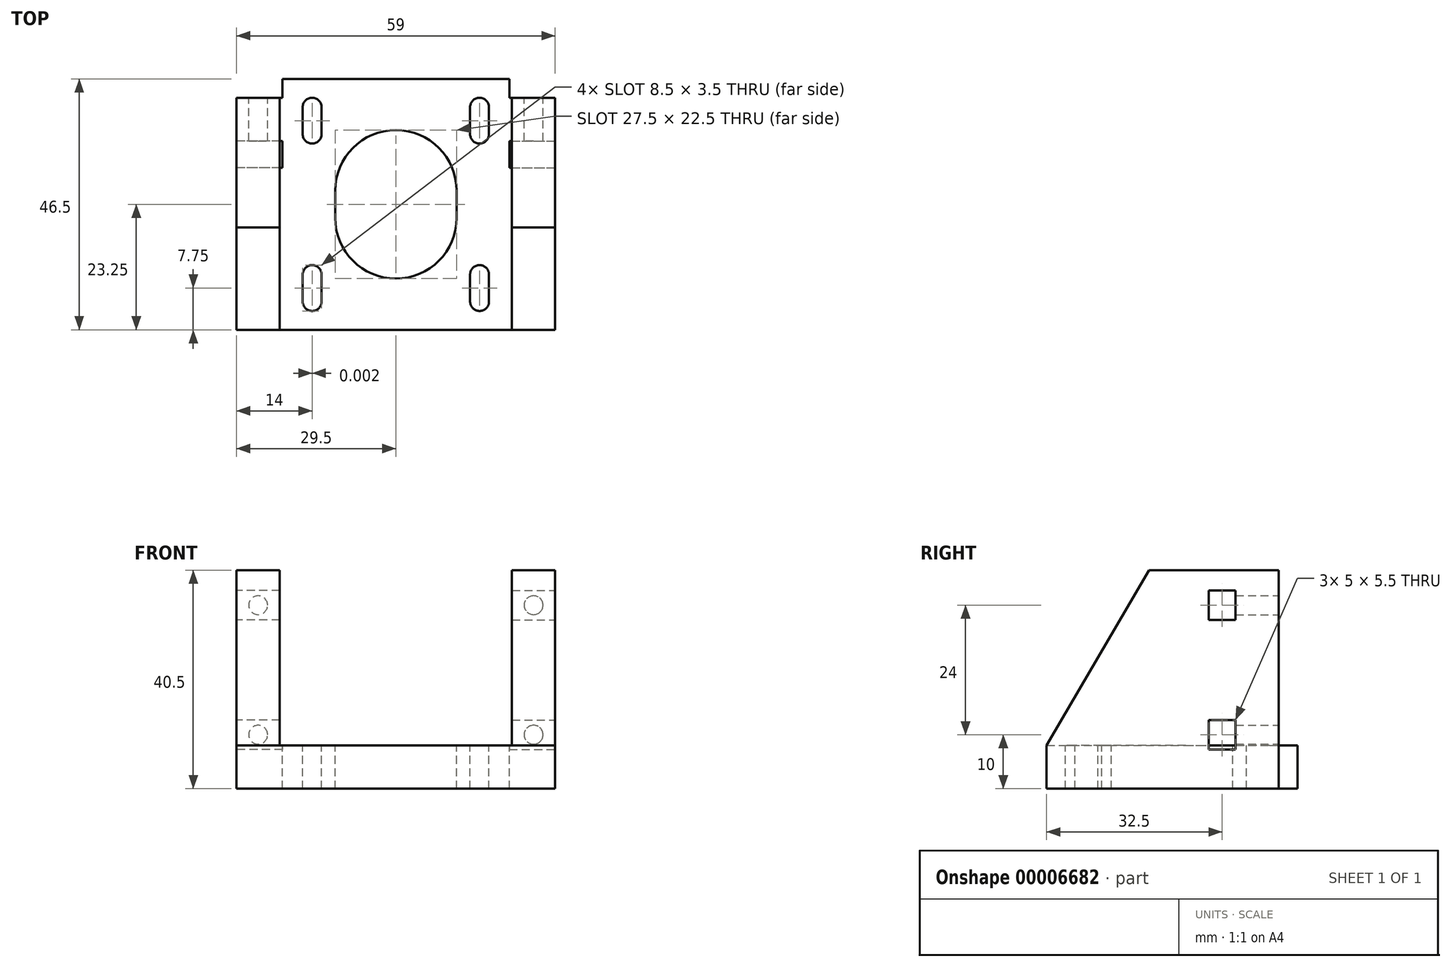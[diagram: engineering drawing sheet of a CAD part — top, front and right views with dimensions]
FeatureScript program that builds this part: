
annotation { "Feature Type Name" : "Feature", "Feature Type Description" : "" }
export const myFeature = defineFeature(function(context is Context, id is Id, definition is map)
    precondition{}
    {
        {
            var Q0;
            Q0=qCreatedBy(makeId("Top.planeOp"),FACE);
            var sketch = newSketch(context, id + "F0", { "sketchPlane" : qUnion([Q0])});
            skLineSegment(sketch, "E0.bottom", {"start": v(0, 0) * mm, "end": v(59, 0) * mm});
            skLineSegment(sketch, "E0.top", {"start": v(0, 46.5) * mm, "end": v(59, 46.5) * mm});
            skLineSegment(sketch, "E0.left", {"start": v(0, 0) * mm, "end": v(0, 46.5) * mm});
            skLineSegment(sketch, "E0.right", {"start": v(59, 0) * mm, "end": v(59, 46.5) * mm});
            skSolve(sketch);
        }
        {
            var Q0;
            Q0 = qSketchRegion(id + "F0", true);
            extrude(context, id + "F1", {"entities" : qUnion([Q0]), "depth" : 40.5 * mm});
        }
        {
            var Q0;
            Q0=makeQuery(id+"F1.opExtrude","CAP_FACE",FACE,{"disambiguationData":[OSD([sQuery(id+"F0.wireOp",EDGE,"E0.bottom"),sQuery(id+"F0.wireOp",EDGE,"E0.top"),sQuery(id+"F0.wireOp",EDGE,"E0.left"),sQuery(id+"F0.wireOp",EDGE,"E0.right")])],"isStart":false});
            var sketch = newSketch(context, id + "F2", { "sketchPlane" : qUnion([Q0])});
            skLineSegment(sketch, "E1.bottom", {"start": v(8, 0) * mm, "end": v(51, 0) * mm});
            skLineSegment(sketch, "E1.top", {"start": v(8, 46.5) * mm, "end": v(51, 46.5) * mm});
            skLineSegment(sketch, "E1.left", {"start": v(8, 0) * mm, "end": v(8, 46.5) * mm});
            skLineSegment(sketch, "E1.right", {"start": v(51, 0) * mm, "end": v(51, 46.5) * mm});
            skSolve(sketch);
        }
        {
            var Q0;
            Q0 = qSketchRegion(id + "F2", true);
            extrude(context, id + "F3", {"entities" : qUnion([Q0]), "operationType" : NewBodyOperationType.REMOVE, "oppositeDirection" : true, "depth" : 32.5 * mm});
        }
        {
            var Q0;
            Q0=makeQuery(id+"F1.opExtrude","SWEPT_FACE",FACE,{"disambiguationData":[OSD([sQuery(id+"F0.wireOp",EDGE,"E0.right")])]});
            var sketch = newSketch(context, id + "F4", { "sketchPlane" : qUnion([Q0])});
            skLineSegment(sketch, "E2", {"start": v(0, 8) * mm, "end": v(19, 40.5) * mm});
            skLineSegment(sketch, "E3", {"start": v(19, 40.5) * mm, "end": v(0, 40.5) * mm});
            skLineSegment(sketch, "E4", {"start": v(0, 40.5) * mm, "end": v(0, 8) * mm});
            skSolve(sketch);
        }
        {
            var Q0;
            Q0 = qSketchRegion(id + "F4", true);
            extrude(context, id + "F5", {"entities" : qUnion([Q0]), "operationType" : NewBodyOperationType.REMOVE, "endBound" : BoundingType.THROUGH_ALL, "oppositeDirection" : true, "depth" : 25 * mm});
        }
        {
            var Q0;
            {var subQ0=sQuery(id+"F0.wireOp",EDGE,"E0.bottom");var subQ1=sQuery(id+"F0.wireOp",EDGE,"E0.top");var subQ2=sQuery(id+"F0.wireOp",EDGE,"E0.left");Q0=makeQuery(id+"F3.boolean.opBoolean","SPLIT",FACE,{"disambiguationData":[TD([makeQuery(id+"F1.opExtrude","SWEPT_FACE",FACE,{"disambiguationData":[OSD([subQ2])]})])],"derivedFrom":makeQuery(id+"F1.opExtrude","CAP_FACE",FACE,{"disambiguationData":[OSD([subQ0,subQ1,subQ2,sQuery(id+"F0.wireOp",EDGE,"E0.right")])],"isStart":false})});}
            var sketch = newSketch(context, id + "F6", { "sketchPlane" : qUnion([Q0])});
            skLineSegment(sketch, "E5.bottom", {"start": v(0, 46.5) * mm, "end": v(8.5, 46.5) * mm});
            skLineSegment(sketch, "E5.top", {"start": v(0, 43) * mm, "end": v(8.5, 43) * mm});
            skLineSegment(sketch, "E5.left", {"start": v(0, 46.5) * mm, "end": v(0, 43) * mm});
            skLineSegment(sketch, "E5.right", {"start": v(8.5, 46.5) * mm, "end": v(8.5, 43) * mm});
            skSolve(sketch);
        }
        {
            var Q0;
            Q0 = qSketchRegion(id + "F6", true);
            extrude(context, id + "F7", {"entities" : qUnion([Q0]), "operationType" : NewBodyOperationType.REMOVE, "endBound" : BoundingType.THROUGH_ALL, "oppositeDirection" : true, "depth" : 25 * mm});
        }
        {
            var Q0;
            {var subQ0=sQuery(id+"F0.wireOp",EDGE,"E0.bottom");var subQ1=sQuery(id+"F0.wireOp",EDGE,"E0.top");var subQ2=sQuery(id+"F0.wireOp",EDGE,"E0.right");Q0=makeQuery(id+"F3.boolean.opBoolean","SPLIT",FACE,{"disambiguationData":[TD([makeQuery(id+"F1.opExtrude","SWEPT_FACE",FACE,{"disambiguationData":[OSD([subQ2])]})])],"derivedFrom":makeQuery(id+"F1.opExtrude","CAP_FACE",FACE,{"disambiguationData":[OSD([subQ0,subQ1,sQuery(id+"F0.wireOp",EDGE,"E0.left"),subQ2])],"isStart":false})});}
            var sketch = newSketch(context, id + "F8", { "sketchPlane" : qUnion([Q0])});
            skLineSegment(sketch, "E6.bottom", {"start": v(59, 46.5) * mm, "end": v(50.5, 46.5) * mm});
            skLineSegment(sketch, "E6.top", {"start": v(59, 43) * mm, "end": v(50.5, 43) * mm});
            skLineSegment(sketch, "E6.left", {"start": v(59, 46.5) * mm, "end": v(59, 43) * mm});
            skLineSegment(sketch, "E6.right", {"start": v(50.5, 46.5) * mm, "end": v(50.5, 43) * mm});
            skSolve(sketch);
        }
        {
            var Q0;
            Q0 = qSketchRegion(id + "F8", true);
            extrude(context, id + "F9", {"entities" : qUnion([Q0]), "operationType" : NewBodyOperationType.REMOVE, "endBound" : BoundingType.THROUGH_ALL, "oppositeDirection" : true, "depth" : 25 * mm});
        }
        {
            var Q0;
            Q0=makeQuery(id+"F1.opExtrude","SWEPT_FACE",FACE,{"disambiguationData":[OSD([sQuery(id+"F0.wireOp",EDGE,"E0.right")])]});
            var sketch = newSketch(context, id + "F10", { "sketchPlane" : qUnion([Q0])});
            skLineSegment(sketch, "E7.bottom", {"start": v(30, 36.75) * mm, "end": v(35, 36.75) * mm});
            skLineSegment(sketch, "E7.top", {"start": v(30, 7.25) * mm, "end": v(35, 7.25) * mm});
            skLineSegment(sketch, "E7.left", {"start": v(30, 36.75) * mm, "end": v(30, 31.25) * mm});
            skLineSegment(sketch, "E7.right", {"start": v(35, 36.75) * mm, "end": v(35, 31.25) * mm});
            skLineSegment(sketch, "E8.0", {"start": v(30, 31.25) * mm, "end": v(35, 31.25) * mm});
            skLineSegment(sketch, "E9.0", {"start": v(30, 12.75) * mm, "end": v(35, 12.75) * mm});
            skLineSegment(sketch, "E10.trimOffspring", {"start": v(30, 12.75) * mm, "end": v(30, 7.25) * mm});
            skLineSegment(sketch, "E11.trimOffspring", {"start": v(35, 12.75) * mm, "end": v(35, 7.25) * mm});
            skSolve(sketch);
        }
        {
            var Q0;
            Q0 = qSketchRegion(id + "F10", true);
            extrude(context, id + "F11", {"entities" : qUnion([Q0]), "operationType" : NewBodyOperationType.REMOVE, "oppositeDirection" : true, "depth" : 8.5 * mm});
        }
        {
            var Q0;
            Q0=makeQuery(id+"F1.opExtrude","SWEPT_FACE",FACE,{"disambiguationData":[OSD([sQuery(id+"F0.wireOp",EDGE,"E0.left")])]});
            var sketch = newSketch(context, id + "F12", { "sketchPlane" : qUnion([Q0])});
            skLineSegment(sketch, "E12.bottom", {"start": v(-35, 36.75) * mm, "end": v(-30, 36.75) * mm});
            skLineSegment(sketch, "E12.top", {"start": v(-35, 7.25) * mm, "end": v(-30, 7.25) * mm});
            skLineSegment(sketch, "E12.left", {"start": v(-35, 36.75) * mm, "end": v(-35, 31.25) * mm});
            skLineSegment(sketch, "E12.right", {"start": v(-30, 36.75) * mm, "end": v(-30, 31.25) * mm});
            skLineSegment(sketch, "E13.0", {"start": v(-35, 31.25) * mm, "end": v(-30, 31.25) * mm});
            skLineSegment(sketch, "E14.0", {"start": v(-35, 12.75) * mm, "end": v(-30, 12.75) * mm});
            skLineSegment(sketch, "E15.trimOffspring", {"start": v(-35, 12.75) * mm, "end": v(-35, 7.25) * mm});
            skLineSegment(sketch, "E16.trimOffspring", {"start": v(-30, 12.75) * mm, "end": v(-30, 7.25) * mm});
            skSolve(sketch);
        }
        {
            var Q0;
            Q0 = qSketchRegion(id + "F12", true);
            extrude(context, id + "F13", {"entities" : qUnion([Q0]), "operationType" : NewBodyOperationType.REMOVE, "oppositeDirection" : true, "depth" : 8.5 * mm});
        }
        {
            var Q0;
            Q0=makeQuery(id+"F9.boolean.opBoolean","COPY",FACE,{"derivedFrom":makeQuery(id+"F9.opExtrude","SWEPT_FACE",FACE,{"disambiguationData":[OSD([sQuery(id+"F8.wireOp",EDGE,"E6.top")])]})});
            var sketch = newSketch(context, id + "F14", { "sketchPlane" : qUnion([Q0])});
            skCircle(sketch, "E17", {"center": v(-55, 10) * mm, "radius": 1.75 * mm});
            skCircle(sketch, "E18", {"center": v(-55, 34) * mm, "radius": 1.75 * mm});
            skSolve(sketch);
        }
        {
            var Q0;
            Q0 = qSketchRegion(id + "F14", true);
            extrude(context, id + "F15", {"entities" : qUnion([Q0]), "operationType" : NewBodyOperationType.REMOVE, "oppositeDirection" : true, "depth" : 10 * mm});
        }
        {
            var Q0;
            Q0=makeQuery(id+"F7.boolean.opBoolean","COPY",FACE,{"derivedFrom":makeQuery(id+"F7.opExtrude","SWEPT_FACE",FACE,{"disambiguationData":[OSD([sQuery(id+"F6.wireOp",EDGE,"E5.top")])]})});
            var sketch = newSketch(context, id + "F16", { "sketchPlane" : qUnion([Q0])});
            skCircle(sketch, "E19", {"center": v(-4, 34) * mm, "radius": 1.75 * mm});
            skCircle(sketch, "E20", {"center": v(-4, 10) * mm, "radius": 1.75 * mm});
            skSolve(sketch);
        }
        {
            var Q0;
            Q0 = qSketchRegion(id + "F16", true);
            extrude(context, id + "F17", {"entities" : qUnion([Q0]), "operationType" : NewBodyOperationType.REMOVE, "oppositeDirection" : true, "depth" : 10 * mm});
        }
        {
            var Q0;
            Q0=makeQuery(id+"F3.boolean.opBoolean","COPY",FACE,{"derivedFrom":makeQuery(id+"F3.opExtrude","CAP_FACE",FACE,{"disambiguationData":[OSD([sQuery(id+"F2.wireOp",EDGE,"E1.bottom"),sQuery(id+"F2.wireOp",EDGE,"E1.top"),sQuery(id+"F2.wireOp",EDGE,"E1.left"),sQuery(id+"F2.wireOp",EDGE,"E1.right")])],"isStart":false})});
            var sketch = newSketch(context, id + "F18", { "sketchPlane" : qUnion([Q0])});
            skLineSegment(sketch, "E21", {"start": v(29.5, 46.5) * mm, "end": v(29.5, 0) * mm, "construction": true});
            skLineSegment(sketch, "E22.0", {"start": v(45, 46.5) * mm, "end": v(45, 0) * mm, "construction": true});
            skLineSegment(sketch, "E23.0", {"start": v(14, 46.5) * mm, "end": v(14, 0) * mm, "construction": true});
            skLineSegment(sketch, "E24.0", {"start": v(40.75, 25.75) * mm, "end": v(40.75, 20.75) * mm});
            skLineSegment(sketch, "E25.0", {"start": v(18.25, 25.75) * mm, "end": v(18.25, 20.75) * mm});
            skArc(sketch, "E26", {"start": v(40.75, 25.75) * mm, "mid": v(29.5, 37) * mm, "end": v(18.25, 25.75) * mm});
            skArc(sketch, "E27.trimOffspring", {"start": v(18.25, 20.75) * mm, "mid": v(29.5, 9.5) * mm, "end": v(40.75, 20.75) * mm});
            skLineSegment(sketch, "E28", {"start": v(14, 23.25) * mm, "end": v(45, 23.25) * mm, "construction": true});
            skLineSegment(sketch, "E29.0", {"start": v(14, 7.75) * mm, "end": v(45, 7.75) * mm, "construction": true});
            skLineSegment(sketch, "E30.0", {"start": v(14, 38.75) * mm, "end": v(45, 38.75) * mm, "construction": true});
            skLineSegment(sketch, "E31.0", {"start": v(12.25, 36.25) * mm, "end": v(46.75, 36.25) * mm, "construction": true});
            skLineSegment(sketch, "E32.0", {"start": v(12.25, 41.25) * mm, "end": v(46.75, 41.25) * mm, "construction": true});
            skLineSegment(sketch, "E33.0", {"start": v(14, 5.25) * mm, "end": v(45, 5.25) * mm, "construction": true});
            skLineSegment(sketch, "E34.0", {"start": v(14, 10.25) * mm, "end": v(45, 10.25) * mm, "construction": true});
            skArc(sketch, "E35", {"start": v(15.75, 10.25) * mm, "mid": v(13.98, 12) * mm, "end": v(12.25, 10.22) * mm});
            skArc(sketch, "E36", {"start": v(12.25, 5.25) * mm, "mid": v(14, 3.5) * mm, "end": v(15.75, 5.25) * mm});
            skArc(sketch, "E37", {"start": v(46.75, 10.23) * mm, "mid": v(45, 12) * mm, "end": v(43.25, 10.25) * mm});
            skArc(sketch, "E38", {"start": v(43.25, 5.25) * mm, "mid": v(45, 3.5) * mm, "end": v(46.75, 5.27) * mm});
            skLineSegment(sketch, "E39", {"start": v(12.25, 10.28) * mm, "end": v(12.25, 5.25) * mm});
            skLineSegment(sketch, "E40", {"start": v(15.75, 10.25) * mm, "end": v(15.75, 5.25) * mm});
            skLineSegment(sketch, "E41", {"start": v(43.25, 10.25) * mm, "end": v(43.25, 5.25) * mm});
            skLineSegment(sketch, "E42", {"start": v(46.75, 10.23) * mm, "end": v(46.75, 5.27) * mm});
            skArc(sketch, "E43", {"start": v(15.75, 41.25) * mm, "mid": v(14, 43) * mm, "end": v(12.25, 41.25) * mm});
            skArc(sketch, "E44", {"start": v(12.25, 36.25) * mm, "mid": v(14, 34.5) * mm, "end": v(15.75, 36.25) * mm});
            skArc(sketch, "E45", {"start": v(46.75, 41.25) * mm, "mid": v(45, 43) * mm, "end": v(43.25, 41.25) * mm});
            skArc(sketch, "E46", {"start": v(43.25, 36.25) * mm, "mid": v(45, 34.5) * mm, "end": v(46.75, 36.25) * mm});
            skLineSegment(sketch, "E47", {"start": v(15.75, 41.25) * mm, "end": v(15.75, 36.25) * mm});
            skLineSegment(sketch, "E48", {"start": v(12.25, 41.25) * mm, "end": v(12.25, 36.25) * mm});
            skLineSegment(sketch, "E49", {"start": v(43.25, 41.25) * mm, "end": v(43.25, 36.25) * mm});
            skLineSegment(sketch, "E50", {"start": v(46.75, 41.25) * mm, "end": v(46.75, 36.25) * mm});
            skSolve(sketch);
        }
        {
            var Q0;
            Q0 = qSketchRegion(id + "F18", true);
            extrude(context, id + "F19", {"entities" : qUnion([Q0]), "operationType" : NewBodyOperationType.REMOVE, "endBound" : BoundingType.THROUGH_ALL, "oppositeDirection" : true, "depth" : 25 * mm});
        }
    });
